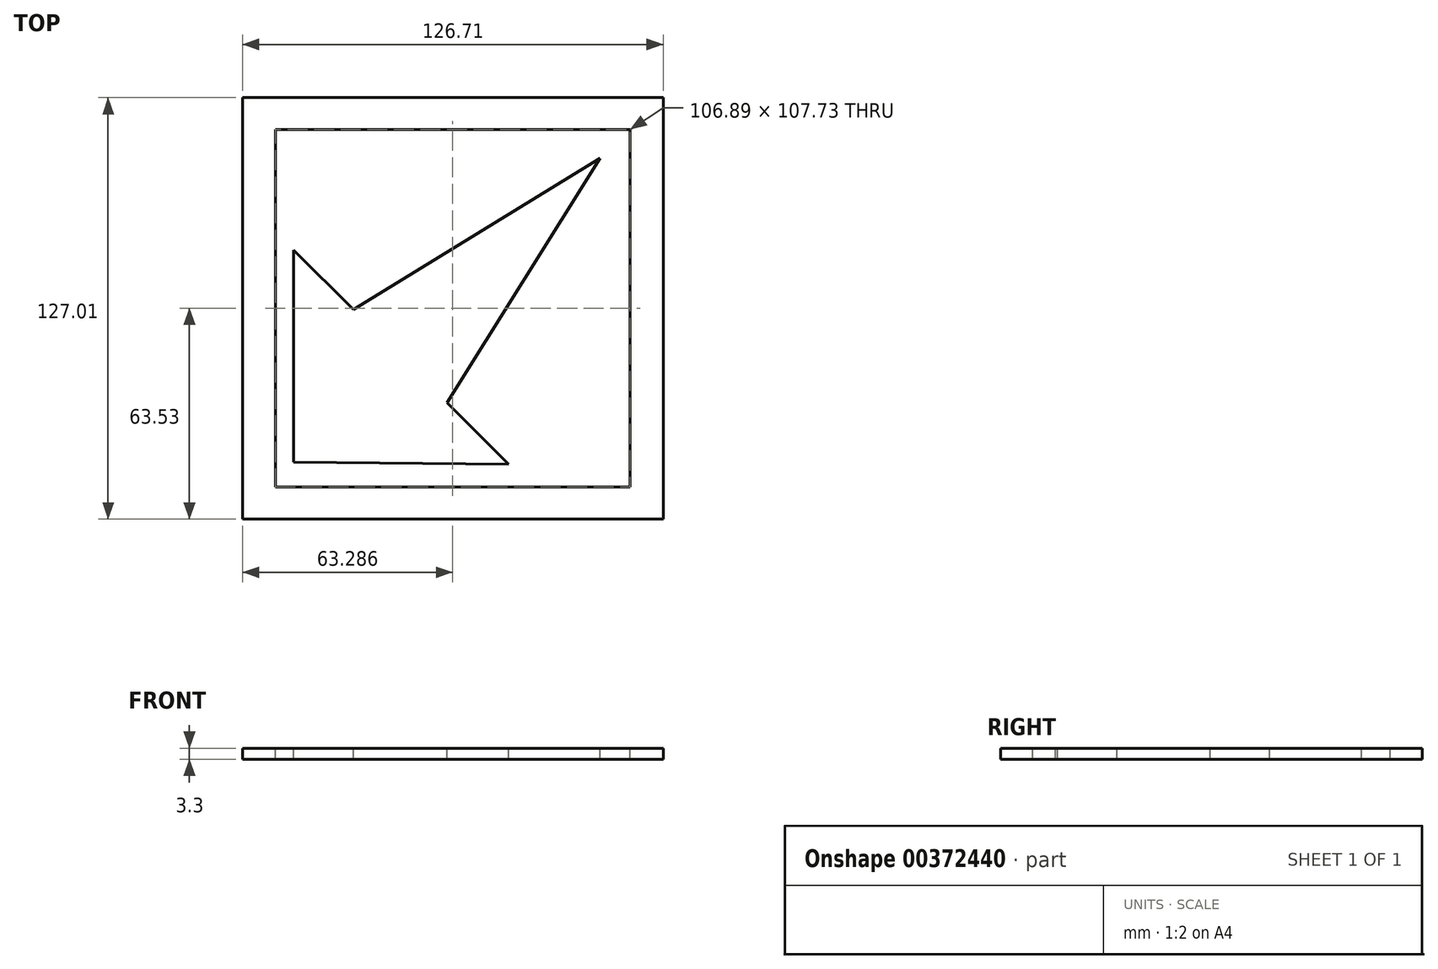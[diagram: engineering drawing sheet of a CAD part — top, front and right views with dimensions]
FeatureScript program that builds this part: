
annotation { "Feature Type Name" : "Feature", "Feature Type Description" : "" }
export const myFeature = defineFeature(function(context is Context, id is Id, definition is map)
    precondition{}
    {
        {
            var Q0;
            Q0=qCreatedBy(makeId("Top.planeOp"),FACE);
            var sketch = newSketch(context, id + "F0", { "sketchPlane" : qUnion([Q0])});
            skLineSegment(sketch, "E0", {"start": v(19.9, 19.33) * mm, "end": v(19.9, 51.65) * mm});
            skLineSegment(sketch, "E1", {"start": v(19.9, 51.65) * mm, "end": v(29.04, 42.58) * mm});
            skLineSegment(sketch, "E2", {"start": v(29.04, 42.58) * mm, "end": v(66.58, 65.64) * mm});
            skLineSegment(sketch, "E3", {"start": v(66.58, 65.64) * mm, "end": v(43.3, 28.4) * mm});
            skLineSegment(sketch, "E4", {"start": v(43.3, 28.4) * mm, "end": v(52.69, 19.02) * mm});
            skLineSegment(sketch, "E5", {"start": v(52.69, 19.02) * mm, "end": v(19.9, 19.33) * mm});
            skLineSegment(sketch, "E6.bottom", {"start": v(12.16, 10.64) * mm, "end": v(76.22, 10.64) * mm});
            skLineSegment(sketch, "E6.top", {"start": v(12.16, 74.85) * mm, "end": v(76.22, 74.85) * mm});
            skLineSegment(sketch, "E6.left", {"start": v(12.16, 10.64) * mm, "end": v(12.16, 74.85) * mm});
            skLineSegment(sketch, "E6.right", {"start": v(76.22, 10.64) * mm, "end": v(76.22, 74.85) * mm});
            skLineSegment(sketch, "E7.bottom", {"start": v(71.17, 70) * mm, "end": v(17.13, 70) * mm});
            skLineSegment(sketch, "E7.top", {"start": v(71.17, 15.53) * mm, "end": v(17.13, 15.53) * mm});
            skLineSegment(sketch, "E7.left", {"start": v(71.17, 70) * mm, "end": v(71.17, 15.53) * mm});
            skLineSegment(sketch, "E7.right", {"start": v(17.13, 70) * mm, "end": v(17.13, 15.53) * mm});
            skSolve(sketch);
        }
        {
            var Q0;
            Q0=makeQuery(id+"F0.imprint","IMPRINT",FACE,{"disambiguationData":[TD([[makeQuery(id+"F0.imprint","IMPRINT",EDGE,{"derivedFrom":sQuery(id+"F0.wireOp",EDGE,"E6.bottom")}),1.0]])]});
            var Q1;
            Q1=makeQuery(id+"F0.imprint","IMPRINT",FACE,{"disambiguationData":[TD([[makeQuery(id+"F0.imprint","IMPRINT",EDGE,{"derivedFrom":sQuery(id+"F0.wireOp",EDGE,"E0")}),-1.0]])]});
            extrude(context, id + "F1", {"entities" : qUnion([Q0, Q1]), "oppositeDirection" : true, "depth" : 1.67 * mm});
        }
        {
            var Q0;
            Q0=makeQuery(id+"F1.opExtrude","SWEPT_BODY",BODY,{"disambiguationData":[OSD([sQuery(id+"F0.wireOp",EDGE,"E6.bottom"),sQuery(id+"F0.wireOp",EDGE,"E6.top"),sQuery(id+"F0.wireOp",EDGE,"E6.left"),sQuery(id+"F0.wireOp",EDGE,"E6.right"),sQuery(id+"F0.wireOp",EDGE,"E7.bottom"),sQuery(id+"F0.wireOp",EDGE,"E7.top"),sQuery(id+"F0.wireOp",EDGE,"E7.left"),sQuery(id+"F0.wireOp",EDGE,"E7.right")])]});
            var Q1;
            Q1=makeQuery(id+"F1.opExtrude","SWEPT_BODY",BODY,{"disambiguationData":[OSD([sQuery(id+"F0.wireOp",EDGE,"E0"),sQuery(id+"F0.wireOp",EDGE,"E1"),sQuery(id+"F0.wireOp",EDGE,"E2"),sQuery(id+"F0.wireOp",EDGE,"E3"),sQuery(id+"F0.wireOp",EDGE,"E4"),sQuery(id+"F0.wireOp",EDGE,"E5")])]});
            var Q2;
            Q2=makeQuery(id+"F1.opExtrude","CAP_VERTEX",VERTEX,{"disambiguationData":[OSD([sQuery(id+"F0.wireOp",EDGE,"E6.bottom"),sQuery(id+"F0.wireOp",EDGE,"E6.left")])],"isStart":false});
            var Q3;
            Q3=qCreatedBy(makeId("Origin.pointOp"),VERTEX);
            transform(context, id + "F2", {"entities" : qUnion([Q0, Q1]), "transformType" : TransformType.TRANSLATION_ENTITY, "oppositeDirectionEntity" : false, "transformLine" : qUnion([Q2, Q3]), "makeCopy" : false});
        }
        {
            var Q0;
            Q0=makeQuery(id+"F1.opExtrude","SWEPT_BODY",BODY,{"disambiguationData":[OSD([sQuery(id+"F0.wireOp",EDGE,"E6.bottom"),sQuery(id+"F0.wireOp",EDGE,"E6.top"),sQuery(id+"F0.wireOp",EDGE,"E6.left"),sQuery(id+"F0.wireOp",EDGE,"E6.right"),sQuery(id+"F0.wireOp",EDGE,"E7.bottom"),sQuery(id+"F0.wireOp",EDGE,"E7.top"),sQuery(id+"F0.wireOp",EDGE,"E7.left"),sQuery(id+"F0.wireOp",EDGE,"E7.right")])]});
            var Q1;
            Q1=makeQuery(id+"F1.opExtrude","SWEPT_BODY",BODY,{"disambiguationData":[OSD([sQuery(id+"F0.wireOp",EDGE,"E0"),sQuery(id+"F0.wireOp",EDGE,"E1"),sQuery(id+"F0.wireOp",EDGE,"E2"),sQuery(id+"F0.wireOp",EDGE,"E3"),sQuery(id+"F0.wireOp",EDGE,"E4"),sQuery(id+"F0.wireOp",EDGE,"E5")])]});
            var Q2;
            Q2=qCreatedBy(makeId("Origin.pointOp"),VERTEX);
            transform(context, id + "F3", {"entities" : qUnion([Q0, Q1]), "transformType" : TransformType.SCALE_UNIFORMLY, "scale" : 1.98, "scalePoint" : qUnion([Q2]), "makeCopy" : false});
        }
        {
            var Q0;
            Q0=qCreatedBy(makeId("Top.planeOp"),FACE);
            var sketch = newSketch(context, id + "F4", { "sketchPlane" : qUnion([Q0])});
            skLineSegment(sketch, "E8.bottom", {"start": v(0, 0) * mm, "end": v(126.71, 0) * mm});
            skLineSegment(sketch, "E8.top", {"start": v(0, 127) * mm, "end": v(126.71, 127) * mm});
            skLineSegment(sketch, "E8.left", {"start": v(0, 0) * mm, "end": v(0, 127) * mm});
            skLineSegment(sketch, "E8.right", {"start": v(126.71, 0) * mm, "end": v(126.71, 127) * mm});
            skSolve(sketch);
        }
        {
            var Q0;
            Q0 = qSketchRegion(id + "F4", true);
            extrude(context, id + "F5", {"entities" : qUnion([Q0]), "depth" : 3.3 * mm});
        }
    });
